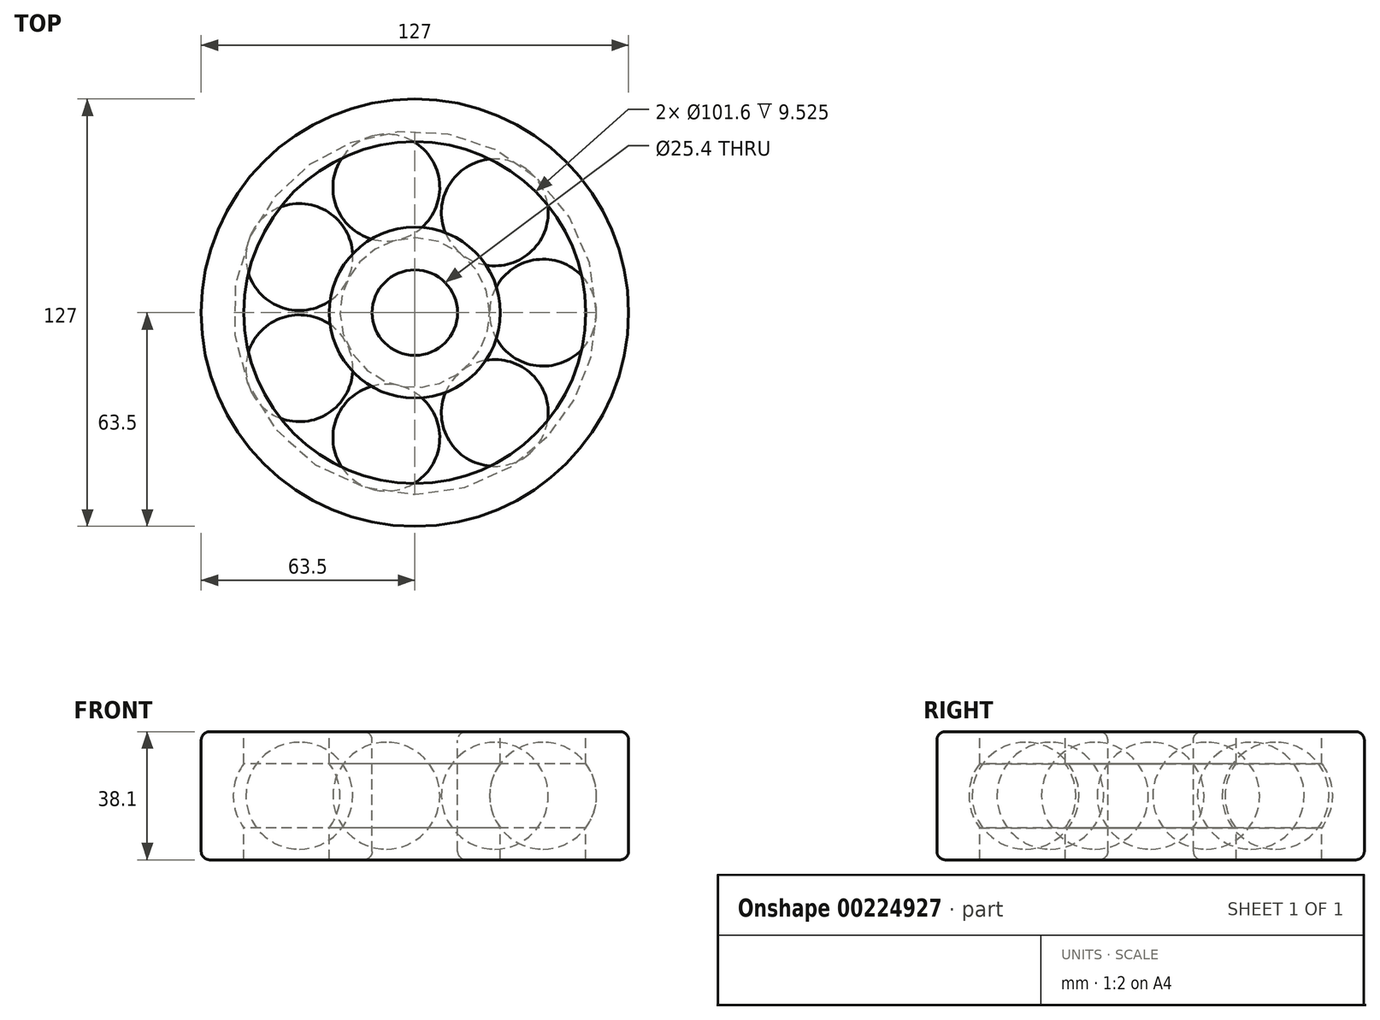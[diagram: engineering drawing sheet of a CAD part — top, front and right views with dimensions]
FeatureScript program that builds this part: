
annotation { "Feature Type Name" : "Feature", "Feature Type Description" : "" }
export const myFeature = defineFeature(function(context is Context, id is Id, definition is map)
    precondition{}
    {
        {
            var Q0;
            Q0=qCreatedBy(makeId("Front.planeOp"),FACE);
            var sketch = newSketch(context, id + "F0", { "sketchPlane" : qUnion([Q0])});
            skLineSegment(sketch, "E0", {"start": v(0, 30.32) * mm, "end": v(0, -37.3) * mm, "construction": true});
            skLineSegment(sketch, "E1.bottom", {"start": v(12.7, 19.05) * mm, "end": v(25.4, 19.05) * mm});
            skLineSegment(sketch, "E1.top", {"start": v(12.7, -19.05) * mm, "end": v(25.4, -19.05) * mm});
            skLineSegment(sketch, "E1.left", {"start": v(12.7, 19.05) * mm, "end": v(12.7, -19.05) * mm});
            skLineSegment(sketch, "E1.right", {"start": v(25.4, 19.05) * mm, "end": v(25.4, -19.05) * mm});
            skCircle(sketch, "E2", {"center": v(38.1, 0) * mm, "radius": 15.88 * mm});
            skLineSegment(sketch, "E3.bottom", {"start": v(50.8, 19.05) * mm, "end": v(63.5, 19.05) * mm});
            skLineSegment(sketch, "E3.top", {"start": v(50.8, -19.05) * mm, "end": v(63.5, -19.05) * mm});
            skLineSegment(sketch, "E3.left", {"start": v(50.8, 19.05) * mm, "end": v(50.8, -19.05) * mm});
            skLineSegment(sketch, "E3.right", {"start": v(63.5, 19.05) * mm, "end": v(63.5, -19.05) * mm});
            skLineSegment(sketch, "E4", {"start": v(3.45, 0) * mm, "end": v(72.7, 0) * mm, "construction": true});
            skPoint(sketch, "E4.endSnap0", {"position": v(63.5, 0) * mm});
            skLineSegment(sketch, "E5", {"start": v(38.1, 15.88) * mm, "end": v(38.1, -15.88) * mm, "construction": true});
            skLineSegment(sketch, "E6", {"start": v(38.1, 15.88) * mm, "end": v(38.1, -15.88) * mm});
            skSolve(sketch);
        }
        {
            var Q0;
            {var subQ1=sQuery(id+"F0.wireOp",EDGE,"E3.bottom");Q0=makeQuery(id+"F0.imprint","IMPRINT",FACE,{"disambiguationData":[TD([[makeQuery(id+"F0.imprint","IMPRINT",EDGE,{"derivedFrom":subQ1}),-1.0]])]});}
            var Q1;
            {var subQ1=sQuery(id+"F0.wireOp",EDGE,"E1.bottom");Q1=makeQuery(id+"F0.imprint","IMPRINT",FACE,{"disambiguationData":[TD([[makeQuery(id+"F0.imprint","IMPRINT",EDGE,{"derivedFrom":subQ1}),-1.0]])]});}
            var Q2;
            Q2=sQuery(id+"F0.wireOp",EDGE,"E0");
            revolve(context, id + "F1", {"entities" : qUnion([Q0, Q1]), "axis" : qUnion([Q2]), "revolveType" : RevolveType.FULL});
        }
        {
            var Q0;
            {var subQ0=sQuery(id+"F0.wireOp",EDGE,"E6");Q0=makeQuery(id+"F0.imprint","IMPRINT",FACE,{"disambiguationData":[TD([[makeQuery(id+"F0.imprint","IMPRINT",EDGE,{"derivedFrom":subQ0}),1.0]])]});}
            var Q1;
            {var subQ0=sQuery(id+"F0.wireOp",EDGE,"E3.left");var subQ1=sQuery(id+"F0.wireOp",EDGE,"E2");var subQ2=makeQuery(id+"F0.imprint","INTERSECT",VERTEX,{"disambiguationData":[OD(0.0)],"derivedFrom":[subQ1,subQ0]});Q1=makeQuery(id+"F0.imprint","IMPRINT",FACE,{"disambiguationData":[TD([[makeQuery(id+"F0.imprint","IMPRINT",EDGE,{"disambiguationData":[TD([[subQ2,1.0]])],"derivedFrom":subQ1}),1.0]])]});}
            var Q2;
            Q2=sQuery(id+"F0.wireOp",EDGE,"E6");
            revolve(context, id + "F2", {"operationType" : NewBodyOperationType.ADD, "entities" : qUnion([Q0, Q1]), "axis" : qUnion([Q2]), "revolveType" : RevolveType.FULL});
        }
        {
            var Q0;
            Q0=makeQuery(id+"F2.opRevolve","SWEPT_BODY",BODY,{"disambiguationData":[OSD([sQuery(id+"F0.wireOp",EDGE,"E2"),sQuery(id+"F0.wireOp",EDGE,"E6")])]});
            var Q1;
            Q1=sQuery(id+"F0.wireOp",EDGE,"E0");
            circularPattern(context, id + "F3", {"entities" : qUnion([Q0]), "axis" : qUnion([Q1]), "angle" : 360 * degree, "instanceCount" : 7, "equalSpace" : true});
        }
        {
            var Q0;
            Q0=makeQuery(id+"F1.opRevolve","SWEPT_EDGE",EDGE,{"disambiguationData":[OSD([sQuery(id+"F0.wireOp",EDGE,"E3.bottom"),sQuery(id+"F0.wireOp",EDGE,"E3.right")])]});
            var Q1;
            Q1=makeQuery(id+"F1.opRevolve","SWEPT_EDGE",EDGE,{"disambiguationData":[OSD([sQuery(id+"F0.wireOp",EDGE,"E3.top"),sQuery(id+"F0.wireOp",EDGE,"E3.right")])]});
            var Q2;
            Q2=makeQuery(id+"F1.opRevolve","SWEPT_EDGE",EDGE,{"disambiguationData":[OSD([sQuery(id+"F0.wireOp",EDGE,"E1.bottom"),sQuery(id+"F0.wireOp",EDGE,"E1.left")])]});
            var Q3;
            Q3=makeQuery(id+"F1.opRevolve","SWEPT_EDGE",EDGE,{"disambiguationData":[OSD([sQuery(id+"F0.wireOp",EDGE,"E1.top"),sQuery(id+"F0.wireOp",EDGE,"E1.left")])]});
            fillet(context, id + "F4", {"entities" : qUnion([Q0, Q1, Q2, Q3]), "radius" : 2.54 * mm, "tangentPropagation" : true, "allowEdgeOverflow" : false});
        }
    });
